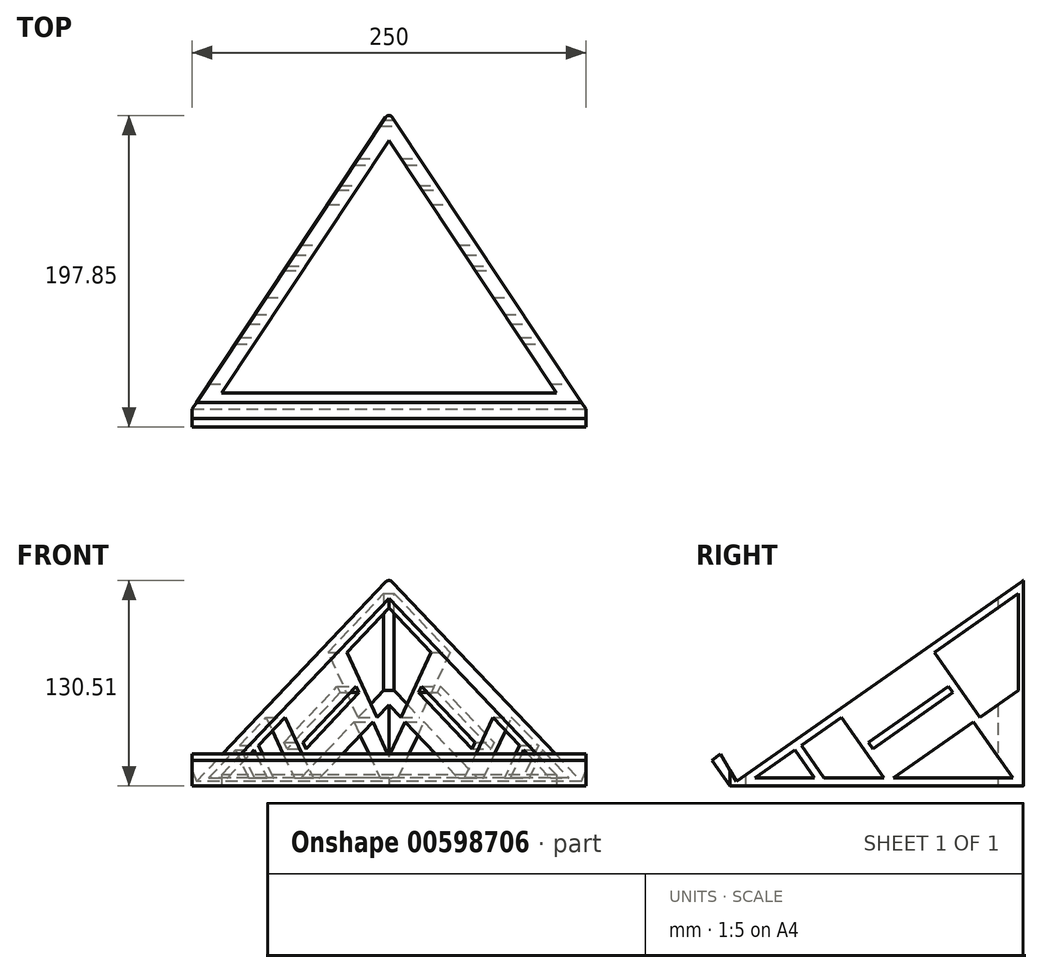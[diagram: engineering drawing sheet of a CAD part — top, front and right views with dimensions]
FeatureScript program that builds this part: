
annotation { "Feature Type Name" : "Feature", "Feature Type Description" : "" }
export const myFeature = defineFeature(function(context is Context, id is Id, definition is map)
    precondition{}
    {
        {
            assignVariable(context, id + "F0", {"name" : "SideWidth", "anyValue" : 5});
        }
        {
            var Q0;
            Q0=qCreatedBy(makeId("Right.planeOp"),FACE);
            var sketch = newSketch(context, id + "F1", { "sketchPlane" : qUnion([Q0])});
            skLineSegment(sketch, "E0", {"start": v(0, 0) * mm, "end": v(188.4, 131.92) * mm});
            skLineSegment(sketch, "E1", {"start": v(188.4, 131.92) * mm, "end": v(188.4, 0) * mm});
            skLineSegment(sketch, "E2", {"start": v(0, 0) * mm, "end": v(188.4, 0) * mm});
            skLineSegment(sketch, "E3", {"start": v(0, 0) * mm, "end": v(0, 131.92) * mm});
            skLineSegment(sketch, "E4", {"start": v(0, 131.92) * mm, "end": v(188.4, 131.92) * mm});
            skLineSegment(sketch, "E5", {"start": v(183.4, 122.32) * mm, "end": v(183.4, 5) * mm});
            skLineSegment(sketch, "E6", {"start": v(183.4, 5) * mm, "end": v(15.86, 5) * mm});
            skLineSegment(sketch, "E7", {"start": v(15.86, 5) * mm, "end": v(183.4, 122.32) * mm});
            skLineSegment(sketch, "E8", {"start": v(41.33, 22.84) * mm, "end": v(53.82, 5) * mm});
            skLineSegment(sketch, "E9", {"start": v(53.82, 5) * mm, "end": v(59.92, 5) * mm});
            skLineSegment(sketch, "E10", {"start": v(59.92, 5) * mm, "end": v(45.43, 25.7) * mm});
            skLineSegment(sketch, "E11", {"start": v(45.43, 25.7) * mm, "end": v(41.33, 22.84) * mm});
            skLineSegment(sketch, "E12", {"start": v(70.9, 43.54) * mm, "end": v(97.89, 5) * mm});
            skLineSegment(sketch, "E13", {"start": v(97.89, 5) * mm, "end": v(104, 5) * mm});
            skLineSegment(sketch, "E14", {"start": v(104, 5) * mm, "end": v(75, 46.4) * mm});
            skLineSegment(sketch, "E15", {"start": v(75, 46.4) * mm, "end": v(70.9, 43.54) * mm});
            skLineSegment(sketch, "E16", {"start": v(183.4, 5) * mm, "end": v(183.4, 8.6) * mm});
            skLineSegment(sketch, "E17", {"start": v(183.4, 8.6) * mm, "end": v(129.97, 84.9) * mm});
            skLineSegment(sketch, "E18", {"start": v(129.97, 84.9) * mm, "end": v(125.87, 82.03) * mm});
            skLineSegment(sketch, "E19", {"start": v(125.87, 82.03) * mm, "end": v(179.81, 5) * mm});
            skLineSegment(sketch, "E20", {"start": v(179.81, 5) * mm, "end": v(183.4, 5) * mm});
            skLineSegment(sketch, "E21", {"start": v(104, 5) * mm, "end": v(183.4, 60.6) * mm});
            skLineSegment(sketch, "E22", {"start": v(183.4, 60.6) * mm, "end": v(183.4, 66.71) * mm});
            skLineSegment(sketch, "E23", {"start": v(183.4, 66.71) * mm, "end": v(101.12, 9.1) * mm});
            skLineSegment(sketch, "E24", {"start": v(101.12, 9.1) * mm, "end": v(104, 5) * mm});
            skLineSegment(sketch, "E25", {"start": v(183.4, 122.32) * mm, "end": v(183.4, 63.66) * mm});
            skLineSegment(sketch, "E26", {"start": v(15.86, 5) * mm, "end": v(41.33, 22.84) * mm});
            skLineSegment(sketch, "E27", {"start": v(45.43, 25.7) * mm, "end": v(70.9, 43.54) * mm});
            skLineSegment(sketch, "E28", {"start": v(41.33, 22.84) * mm, "end": v(15.86, 5) * mm});
            skLineSegment(sketch, "E29", {"start": v(88.06, 27.75) * mm, "end": v(138.94, 63.38) * mm});
            skLineSegment(sketch, "E30", {"start": v(138.94, 63.38) * mm, "end": v(141.8, 59.28) * mm});
            skLineSegment(sketch, "E31", {"start": v(141.8, 59.28) * mm, "end": v(90.93, 23.66) * mm});
            skLineSegment(sketch, "E32", {"start": v(90.93, 23.66) * mm, "end": v(88.06, 27.75) * mm});
            skLineSegment(sketch, "E33", {"start": v(75, 46.4) * mm, "end": v(89.5, 25.7) * mm});
            skLineSegment(sketch, "E34", {"start": v(158.74, 105.04) * mm, "end": v(183.4, 69.81) * mm});
            skLineSegment(sketch, "E35", {"start": v(183.4, 69.81) * mm, "end": v(183.4, 66.71) * mm});
            skLineSegment(sketch, "E36", {"start": v(180.77, 64.86) * mm, "end": v(154.64, 102.18) * mm});
            skLineSegment(sketch, "E37", {"start": v(154.64, 102.18) * mm, "end": v(158.74, 105.04) * mm});
            skLineSegment(sketch, "E38", {"start": v(129.97, 84.9) * mm, "end": v(156.69, 103.61) * mm});
            skLineSegment(sketch, "E39", {"start": v(183.4, 122.32) * mm, "end": v(129.97, 84.9) * mm});
            skLineSegment(sketch, "E40", {"start": v(0, 0) * mm, "end": v(-11.47, 16.38) * mm});
            skLineSegment(sketch, "E41", {"start": v(-11.47, 16.38) * mm, "end": v(-5.94, 20.25) * mm});
            skLineSegment(sketch, "E42", {"start": v(-5.94, 20.25) * mm, "end": v(4.1, 2.87) * mm});
            skSolve(sketch);
        }
        {
            var Q0;
            Q0=qCreatedBy(makeId("Top.planeOp"),FACE);
            var sketch = newSketch(context, id + "F2", { "sketchPlane" : qUnion([Q0])});
            skLineSegment(sketch, "E43", {"start": v(-125, 0) * mm, "end": v(125, 0) * mm});
            skLineSegment(sketch, "E44", {"start": v(125, 0) * mm, "end": v(0, 188.4) * mm});
            skLineSegment(sketch, "E45", {"start": v(0, 188.4) * mm, "end": v(-125, 0) * mm});
            skLineSegment(sketch, "E46", {"start": v(-106.36, 10) * mm, "end": v(106.36, 10) * mm});
            skLineSegment(sketch, "E47", {"start": v(106.36, 10) * mm, "end": v(0, 170.32) * mm});
            skLineSegment(sketch, "E48", {"start": v(0, 170.32) * mm, "end": v(-106.36, 10) * mm});
            skLineSegment(sketch, "E49", {"start": v(-125, 0) * mm, "end": v(-125, 188.4) * mm});
            skLineSegment(sketch, "E50", {"start": v(-125, 188.4) * mm, "end": v(0, 188.4) * mm});
            skLineSegment(sketch, "E51", {"start": v(125, 188.4) * mm, "end": v(0, 188.4) * mm});
            skLineSegment(sketch, "E52", {"start": v(125, 188.4) * mm, "end": v(125, 0) * mm});
            skSolve(sketch);
        }
        {
            var Q0;
            Q0=makeQuery(id+"F2.imprint","IMPRINT",FACE,{"disambiguationData":[TD([[makeQuery(id+"F2.imprint","IMPRINT",EDGE,{"derivedFrom":sQuery(id+"F2.wireOp",EDGE,"E43")}),1.0]])]});
            var Q1;
            Q1=sQuery(id+"F1.wireOp",VERTEX,"E1.start");
            extrude(context, id + "F3", {"entities" : qUnion([Q0]), "endBound" : BoundingType.UP_TO_VERTEX, "depth" : 25 * mm, "endBoundEntityVertex" : qUnion([Q1]), "offsetDistance" : 25 * mm});
        }
        {
            var Q0;
            {var subQ2=sQuery(id+"F1.wireOp",EDGE,"E8");Q0=makeQuery(id+"F1.imprint","IMPRINT",FACE,{"disambiguationData":[TD([[makeQuery(id+"F1.imprint","IMPRINT",EDGE,{"derivedFrom":subQ2}),-1.0]])]});}
            var Q1;
            {var subQ0=sQuery(id+"F1.wireOp",EDGE,"E10");Q1=makeQuery(id+"F1.imprint","IMPRINT",FACE,{"disambiguationData":[TD([[makeQuery(id+"F1.imprint","IMPRINT",EDGE,{"derivedFrom":subQ0}),-1.0]])]});}
            var Q2;
            {var subQ0=sQuery(id+"F1.wireOp",EDGE,"E7");Q2=makeQuery(id+"F1.imprint","IMPRINT",FACE,{"disambiguationData":[TD([[makeQuery(id+"F1.imprint","IMPRINT",EDGE,{"derivedFrom":subQ0}),-1.0]])]});}
            var Q3;
            {var subQ0=sQuery(id+"F1.wireOp",EDGE,"E14");Q3=makeQuery(id+"F1.imprint","IMPRINT",FACE,{"disambiguationData":[TD([[makeQuery(id+"F1.imprint","IMPRINT",EDGE,{"derivedFrom":subQ0}),-1.0]])]});}
            var Q4;
            {var subQ0=sQuery(id+"F1.wireOp",EDGE,"E19");var subQ3=sQuery(id+"F1.wireOp",EDGE,"E21");var subQ5=makeQuery(id+"F1.imprint","INTERSECT",VERTEX,{"derivedFrom":[subQ0,subQ3]});Q4=makeQuery(id+"F1.imprint","IMPRINT",FACE,{"disambiguationData":[TD([[makeQuery(id+"F1.imprint","IMPRINT",EDGE,{"disambiguationData":[TD([[subQ5,-1.0]])],"derivedFrom":subQ0}),-1.0]])]});}
            var Q5;
            {var subQ0=sQuery(id+"F1.wireOp",EDGE,"E5");Q5=makeQuery(id+"F1.imprint","IMPRINT",FACE,{"disambiguationData":[TD([[makeQuery(id+"F1.imprint","IMPRINT",EDGE,{"derivedFrom":subQ0}),-1.0]])]});}
            var Q6;
            {var subQ5=sQuery(id+"F1.wireOp",EDGE,"E36");Q6=makeQuery(id+"F1.imprint","IMPRINT",FACE,{"disambiguationData":[TD([[makeQuery(id+"F1.imprint","IMPRINT",EDGE,{"derivedFrom":subQ5}),1.0]])]});}
            var Q7;
            {var subQ3=sQuery(id+"F1.wireOp",EDGE,"E34");Q7=makeQuery(id+"F1.imprint","IMPRINT",FACE,{"disambiguationData":[TD([[makeQuery(id+"F1.imprint","IMPRINT",EDGE,{"derivedFrom":subQ3}),1.0]])]});}
            var Q8;
            Q8=makeQuery(id+"F1.imprint","IMPRINT",FACE,{"disambiguationData":[TD([[makeQuery(id+"F1.imprint","IMPRINT",EDGE,{"derivedFrom":sQuery(id+"F1.wireOp",EDGE,"E0")}),1.0]])]});
            var Q9;
            {var subQ0=sQuery(id+"F1.wireOp",EDGE,"E4");Q9=makeQuery(id+"F1.imprint","IMPRINT",FACE,{"disambiguationData":[TD([[makeQuery(id+"F1.imprint","IMPRINT",EDGE,{"derivedFrom":subQ0}),-1.0]])]});}
            extrude(context, id + "F4", {"entities" : qUnion([Q0, Q1, Q2, Q3, Q4, Q5, Q6, Q7, Q8, Q9]), "operationType" : NewBodyOperationType.REMOVE, "endBound" : BoundingType.THROUGH_ALL, "oppositeDirection" : true, "depth" : 25 * mm, "offsetDistance" : 25 * mm, "hasSecondDirection" : true, "secondDirectionBound" : BoundingType.THROUGH_ALL, "secondDirectionOppositeDirection" : false, "secondDirectionDepth" : 25 * mm});
        }
        {
            var Q0;
            {var subQ0=sQuery(id+"F1.wireOp",EDGE,"E40");Q0=makeQuery(id+"F1.imprint","IMPRINT",FACE,{"disambiguationData":[TD([[makeQuery(id+"F1.imprint","IMPRINT",EDGE,{"derivedFrom":subQ0}),-1.0]])]});}
            var Q1;
            {var subQ1=sQuery(id+"F1.wireOp",EDGE,"E0");var subQ3=sQuery(id+"F1.wireOp",EDGE,"E42");var subQ4=makeQuery(id+"F1.imprint","INTERSECT",VERTEX,{"derivedFrom":[subQ1,subQ3]});Q1=makeQuery(id+"F1.imprint","IMPRINT",FACE,{"disambiguationData":[TD([[makeQuery(id+"F1.imprint","IMPRINT",EDGE,{"disambiguationData":[TD([[subQ4,1.0]])],"derivedFrom":subQ3}),-1.0]])]});}
            var Q2;
            Q2=makeQuery(id+"F3.opExtrude","CAP_VERTEX",VERTEX,{"disambiguationData":[OSD([sQuery(id+"F2.wireOp",EDGE,"E43"),sQuery(id+"F2.wireOp",EDGE,"E44")])],"isStart":true});
            var Q3;
            Q3=makeQuery(id+"F3.opExtrude","CAP_VERTEX",VERTEX,{"disambiguationData":[OSD([sQuery(id+"F2.wireOp",EDGE,"E43"),sQuery(id+"F2.wireOp",EDGE,"E45")])],"isStart":true});
            extrude(context, id + "F5", {"entities" : qUnion([Q0, Q1]), "operationType" : NewBodyOperationType.ADD, "endBound" : BoundingType.UP_TO_VERTEX, "depth" : 25 * mm, "endBoundEntityVertex" : qUnion([Q2]), "offsetDistance" : 25 * mm, "hasSecondDirection" : true, "secondDirectionBound" : BoundingType.UP_TO_VERTEX, "secondDirectionOppositeDirection" : true, "secondDirectionDepth" : 25 * mm, "secondDirectionBoundEntityVertex" : qUnion([Q3])});
        }
        {
            var Q0;
            Q0=makeQuery(id+"F2.imprint","IMPRINT",FACE,{"disambiguationData":[TD([[makeQuery(id+"F2.imprint","IMPRINT",EDGE,{"derivedFrom":sQuery(id+"F2.wireOp",EDGE,"E45")}),-1.0]])]});
            var Q1;
            Q1=makeQuery(id+"F2.imprint","IMPRINT",FACE,{"disambiguationData":[TD([[makeQuery(id+"F2.imprint","IMPRINT",EDGE,{"derivedFrom":sQuery(id+"F2.wireOp",EDGE,"E44")}),-1.0]])]});
            extrude(context, id + "F6", {"entities" : qUnion([Q0, Q1]), "operationType" : NewBodyOperationType.REMOVE, "endBound" : BoundingType.THROUGH_ALL, "depth" : 25 * mm, "offsetDistance" : 25 * mm});
        }
        {
            var Q0;
            Q0=makeQuery(id+"F5.opExtrude","TWEAK_EDGE",EDGE,{"derivedFrom":[makeQuery(id+"F1.imprint","IMPRINT",EDGE,{"derivedFrom":sQuery(id+"F1.wireOp",EDGE,"E40")}),makeQuery(id+"F1.imprint","IMPRINT",EDGE,{"derivedFrom":sQuery(id+"F1.wireOp",EDGE,"E41")})]});
            var Q1;
            Q1=makeQuery(id+"F5.opExtrude","TWEAK_EDGE",EDGE,{"derivedFrom":[makeQuery(id+"F1.imprint","IMPRINT",EDGE,{"derivedFrom":sQuery(id+"F1.wireOp",EDGE,"E41")}),dummyQuery(id+"F5.secondVertexPlane.planeOp",FACE)]});
            var Q2;
            Q2=makeQuery(id+"F5.opExtrude","TWEAK_EDGE",EDGE,{"derivedFrom":[makeQuery(id+"F1.imprint","IMPRINT",EDGE,{"derivedFrom":sQuery(id+"F1.wireOp",EDGE,"E41")}),dummyQuery(id+"F5.vertexPlane.planeOp",FACE)]});
            var Q3;
            Q3=makeQuery(id+"F5.opExtrude","TWEAK_EDGE",EDGE,{"derivedFrom":[makeQuery(id+"F1.imprint","IMPRINT",EDGE,{"derivedFrom":sQuery(id+"F1.wireOp",EDGE,"E40")}),dummyQuery(id+"F5.vertexPlane.planeOp",FACE)]});
            var Q4;
            Q4=makeQuery(id+"F5.opExtrude","TWEAK_EDGE",EDGE,{"derivedFrom":[makeQuery(id+"F1.imprint","IMPRINT",EDGE,{"derivedFrom":sQuery(id+"F1.wireOp",EDGE,"E40")}),dummyQuery(id+"F5.secondVertexPlane.planeOp",FACE)]});
            var Q5;
            Q5=makeQuery(id+"F3.opExtrude","SWEPT_EDGE",EDGE,{"disambiguationData":[OSD([sQuery(id+"F2.wireOp",EDGE,"E44"),sQuery(id+"F2.wireOp",EDGE,"E45"),sQuery(id+"F2.wireOp",EDGE,"E50"),sQuery(id+"F2.wireOp",EDGE,"E51")])]});
            var Q6;
            Q6=makeQuery(id+"F5.opExtrude","CAP_FACE",FACE,{"disambiguationData":[OSD([dummyQuery(id+"F5.secondVertexPlane.planeOp",FACE)])],"isStart":true});
            var Q7;
            Q7=makeQuery(id+"F5.opExtrude","CAP_FACE",FACE,{"disambiguationData":[OSD([dummyQuery(id+"F5.vertexPlane.planeOp",FACE)])],"isStart":false});
            fillet(context, id + "F7", {"entities" : qUnion([Q0, Q1, Q2, Q3, Q4, Q5, Q6, Q7]), "radius" : (getVariable(context, 'SideWidth') / 2) * mm, "tangentPropagation" : true, "allowEdgeOverflow" : false});
        }
    });
